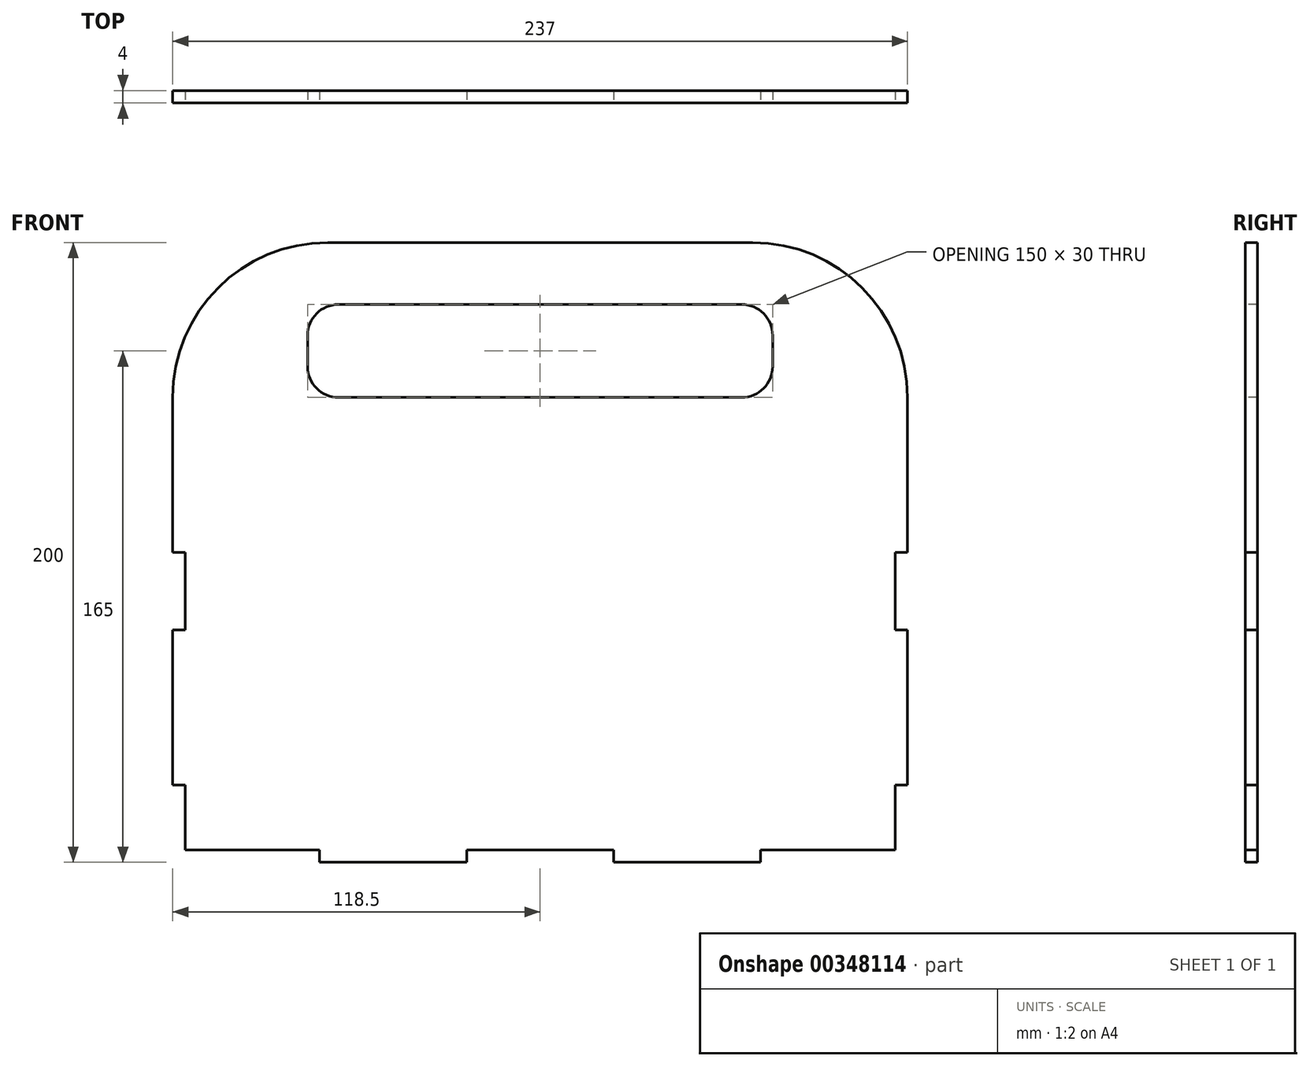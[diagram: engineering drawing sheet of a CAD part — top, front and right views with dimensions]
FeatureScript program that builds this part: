
annotation { "Feature Type Name" : "Feature", "Feature Type Description" : "" }
export const myFeature = defineFeature(function(context is Context, id is Id, definition is map)
    precondition{}
    {
        {
            var Q0;
            Q0=qCreatedBy(makeId("Front.planeOp"),FACE);
            var sketch = newSketch(context, id + "F0", { "sketchPlane" : qUnion([Q0])});
            skLineSegment(sketch, "E0.bottom", {"start": v(0, 0) * mm, "end": v(237, 0) * mm});
            skLineSegment(sketch, "E0.top", {"start": v(50, 200) * mm, "end": v(187, 200) * mm});
            skLineSegment(sketch, "E0.left", {"start": v(0, 0) * mm, "end": v(0, 150) * mm});
            skLineSegment(sketch, "E0.right", {"start": v(237, 0) * mm, "end": v(237, 150) * mm});
            skPoint(sketch, "E1.visualSharp", {"position": v(0, 200) * mm});
            skArc(sketch, "E1.filletArc", {"start": v(50, 200) * mm, "mid": v(14.64, 185.36) * mm, "end": v(0, 150) * mm});
            skPoint(sketch, "E2.visualSharp", {"position": v(237, 200) * mm});
            skArc(sketch, "E2.filletArc", {"start": v(237, 150) * mm, "mid": v(222.36, 185.36) * mm, "end": v(187, 200) * mm});
            skSolve(sketch);
        }
        {
            var Q0;
            Q0 = qSketchRegion(id + "F0", true);
            extrude(context, id + "F1", {"entities" : qUnion([Q0]), "depth" : 4 * mm});
        }
        {
            var Q0;
            Q0=makeQuery(id+"F1.opExtrude","CAP_FACE",FACE,{"disambiguationData":[OSD([sQuery(id+"F0.wireOp",EDGE,"E0.bottom"),sQuery(id+"F0.wireOp",EDGE,"E0.top"),sQuery(id+"F0.wireOp",EDGE,"E0.left"),sQuery(id+"F0.wireOp",EDGE,"E0.right"),sQuery(id+"F0.wireOp",EDGE,"E1.filletArc"),sQuery(id+"F0.wireOp",EDGE,"E2.filletArc")])],"isStart":false});
            var sketch = newSketch(context, id + "F2", { "sketchPlane" : qUnion([Q0])});
            skLineSegment(sketch, "E3.bottom", {"start": v(0, 0) * mm, "end": v(47.4, 0) * mm});
            skLineSegment(sketch, "E3.top", {"start": v(0, 4) * mm, "end": v(47.4, 4) * mm});
            skLineSegment(sketch, "E3.left", {"start": v(0, 0) * mm, "end": v(0, 4) * mm});
            skLineSegment(sketch, "E3.right", {"start": v(47.4, 0) * mm, "end": v(47.4, 4) * mm});
            skLineSegment(sketch, "E4.bottom", {"start": v(94.8, 0) * mm, "end": v(142.2, 0) * mm});
            skLineSegment(sketch, "E4.top", {"start": v(94.8, 4) * mm, "end": v(142.2, 4) * mm});
            skLineSegment(sketch, "E4.left", {"start": v(94.8, 0) * mm, "end": v(94.8, 4) * mm});
            skLineSegment(sketch, "E4.right", {"start": v(142.2, 0) * mm, "end": v(142.2, 4) * mm});
            skLineSegment(sketch, "E5.bottom", {"start": v(237, 0) * mm, "end": v(189.6, 0) * mm});
            skLineSegment(sketch, "E5.top", {"start": v(237, 4) * mm, "end": v(189.6, 4) * mm});
            skLineSegment(sketch, "E5.left", {"start": v(237, 0) * mm, "end": v(237, 4) * mm});
            skLineSegment(sketch, "E5.right", {"start": v(189.6, 0) * mm, "end": v(189.6, 4) * mm});
            skLineSegment(sketch, "E6", {"start": v(47.4, 0) * mm, "end": v(94.8, 0) * mm});
            skLineSegment(sketch, "E7", {"start": v(142.2, 0) * mm, "end": v(189.6, 0) * mm});
            skLineSegment(sketch, "E8", {"start": v(0, 100) * mm, "end": v(237, 100) * mm, "construction": true});
            skLineSegment(sketch, "E9.bottom", {"start": v(0, 100) * mm, "end": v(4, 100) * mm});
            skLineSegment(sketch, "E9.top", {"start": v(0, 75) * mm, "end": v(4, 75) * mm});
            skLineSegment(sketch, "E9.left", {"start": v(0, 100) * mm, "end": v(0, 75) * mm});
            skLineSegment(sketch, "E9.right", {"start": v(4, 100) * mm, "end": v(4, 75) * mm});
            skLineSegment(sketch, "E10.bottom", {"start": v(0, 4) * mm, "end": v(4, 4) * mm});
            skLineSegment(sketch, "E10.top", {"start": v(0, 25) * mm, "end": v(4, 25) * mm});
            skLineSegment(sketch, "E10.left", {"start": v(0, 4) * mm, "end": v(0, 25) * mm});
            skLineSegment(sketch, "E10.right", {"start": v(4, 4) * mm, "end": v(4, 25) * mm});
            skLineSegment(sketch, "E11", {"start": v(118.5, 100) * mm, "end": v(118.5, 4) * mm, "construction": true});
            skLineSegment(sketch, "E12.MirrorCS", {"start": v(237, 4) * mm, "end": v(233, 4) * mm});
            skLineSegment(sketch, "E13.MirrorCS", {"start": v(237, 100) * mm, "end": v(233, 100) * mm});
            skLineSegment(sketch, "E14.MirrorCS", {"start": v(237, 25) * mm, "end": v(233, 25) * mm});
            skLineSegment(sketch, "E15.MirrorCS", {"start": v(237, 75) * mm, "end": v(233, 75) * mm});
            skLineSegment(sketch, "E16.MirrorCS", {"start": v(237, 100) * mm, "end": v(0, 100) * mm, "construction": true});
            skLineSegment(sketch, "E17.MirrorCS", {"start": v(233, 4) * mm, "end": v(233, 25) * mm});
            skLineSegment(sketch, "E18.MirrorCS", {"start": v(233, 100) * mm, "end": v(233, 75) * mm});
            skLineSegment(sketch, "E19.MirrorCS", {"start": v(237, 100) * mm, "end": v(237, 75) * mm});
            skLineSegment(sketch, "E20.MirrorCS", {"start": v(237, 4) * mm, "end": v(237, 25) * mm});
            skSolve(sketch);
        }
        {
            var Q0;
            Q0 = qSketchRegion(id + "F2", true);
            extrude(context, id + "F3", {"entities" : qUnion([Q0]), "operationType" : NewBodyOperationType.REMOVE, "endBound" : BoundingType.UP_TO_NEXT, "oppositeDirection" : true, "depth" : 25 * mm});
        }
        {
            var Q0;
            Q0=makeQuery(id+"F1.opExtrude","CAP_FACE",FACE,{"disambiguationData":[OSD([sQuery(id+"F0.wireOp",EDGE,"E0.bottom"),sQuery(id+"F0.wireOp",EDGE,"E0.top"),sQuery(id+"F0.wireOp",EDGE,"E0.left"),sQuery(id+"F0.wireOp",EDGE,"E0.right"),sQuery(id+"F0.wireOp",EDGE,"E1.filletArc"),sQuery(id+"F0.wireOp",EDGE,"E2.filletArc")])],"isStart":false});
            var sketch = newSketch(context, id + "F4", { "sketchPlane" : qUnion([Q0])});
            skLineSegment(sketch, "E21.bottom", {"start": v(53.5, 180) * mm, "end": v(183.5, 180) * mm});
            skLineSegment(sketch, "E21.top", {"start": v(53.5, 150) * mm, "end": v(183.5, 150) * mm});
            skLineSegment(sketch, "E21.left", {"start": v(43.5, 170) * mm, "end": v(43.5, 160) * mm});
            skLineSegment(sketch, "E21.right", {"start": v(193.5, 170) * mm, "end": v(193.5, 160) * mm});
            skPoint(sketch, "E22.visualSharp", {"position": v(43.5, 180) * mm});
            skArc(sketch, "E22.filletArc", {"start": v(53.5, 180) * mm, "mid": v(46.43, 177.07) * mm, "end": v(43.5, 170) * mm});
            skPoint(sketch, "E23.visualSharp", {"position": v(193.5, 180) * mm});
            skArc(sketch, "E23.filletArc", {"start": v(193.5, 170) * mm, "mid": v(190.57, 177.07) * mm, "end": v(183.5, 180) * mm});
            skPoint(sketch, "E24.visualSharp", {"position": v(193.5, 150) * mm});
            skArc(sketch, "E24.filletArc", {"start": v(183.5, 150) * mm, "mid": v(190.57, 152.93) * mm, "end": v(193.5, 160) * mm});
            skPoint(sketch, "E25.visualSharp", {"position": v(43.5, 150) * mm});
            skArc(sketch, "E25.filletArc", {"start": v(43.5, 160) * mm, "mid": v(46.43, 152.93) * mm, "end": v(53.5, 150) * mm});
            skLineSegment(sketch, "E26", {"start": v(118.5, 200) * mm, "end": v(118.5, 180) * mm, "construction": true});
            skSolve(sketch);
        }
        {
            var Q0;
            Q0 = qSketchRegion(id + "F4", true);
            extrude(context, id + "F5", {"entities" : qUnion([Q0]), "operationType" : NewBodyOperationType.REMOVE, "endBound" : BoundingType.UP_TO_NEXT, "oppositeDirection" : true, "depth" : 25 * mm});
        }
    });
